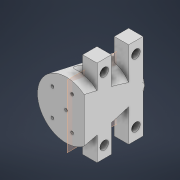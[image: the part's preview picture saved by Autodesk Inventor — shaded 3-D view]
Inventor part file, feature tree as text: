
AUTODESK INVENTOR PART (.ipt)
format: ipt  version: 2022 (Build 260153000, 153)  size: 401,408 bytes
history: native  units: mm
features: sketch x14, extrude x6, sweep x4, plane x3
ambient origin geometry x8: Origin, YZ Plane, XZ Plane, XY Plane, X Axis, Y Axis, Z Axis, Center Point
bodies: Solid1 (feature_tree)
feature tree (27):
  extrude  "Extrusion1"  Depth=21.0mm
  extrude  "Extrusion2"  Depth=1.0mm
  extrude  "Extrusion3"  Depth=3.0mm
  sketch  "Sketch4"  dims[d10=45.0deg d11=1.0mm]
  plane  "Work Plane1"
  sketch  "Sketch5"  dims[d12=90.0deg d18=3.0mm]
  sketch  "Sketch6"  dims[d19=45.0deg d20=1.0mm]
  plane  "Work Plane2"
  sketch  "Sketch7"  dims[d21=90.0deg d27=3.0mm]
  sketch  "Sketch8"  dims[d28=135.0deg d29=5.0mm]
  plane  "Work Plane3"
  extrude  "Extrusion4"  Depth=1.0mm
  sketch  "Sketch10"  dims[d30=45.0deg d31=1.0mm]
  sketch  "Sketch11"  dims[d32=90.0deg d38=3.0mm]
  sketch  "Sketch12"  dims[d39=135.0deg]
  extrude  "Extrusion5"  Depth=3.0mm
  extrude  "Extrusion6"  Depth=1.0mm
  sweep  "Sweep5"
  sweep  "Sweep6"
  sweep  "Sweep7"
  sweep  "Sweep8"
  sketch  "Sketch1"  dims[d1=12.5mm d2=21.0mm d3=1.745329mm]
  sketch  "Sketch2"  dims[d4=21.0mm d5=0.0mm d6=1.0mm]
  sketch  "Sketch3"  dims[d7=21.0mm d8=0.0mm d9=3.0mm]
  sketch  "Sketch15"  dims[d40=1.0mm]
  sketch  "Sketch16"  dims[d46=3.0mm]
  sketch  "Sketch17"  dims[d47=11.0mm d48=5.0mm d49=30.0mm d50=5.0mm d51=30.0mm d52=5.0mm d53=0.0mm d54=4.0mm d55=90.0deg d56=22.0mm d57=11.0mm d58=22.0mm d59=3.0mm d60=3.0mm d61=3.0mm d62=3.0mm d63=5.0mm d64=0.0mm d65=5.9mm d66=5.9mm d67=55.0mm d68=0.0mm d74=0.0mm d75=0.0mm d79=0.0mm d80=0.0mm d84=0.0mm d85=0.0mm d89=0.0mm d90=0.0mm]
